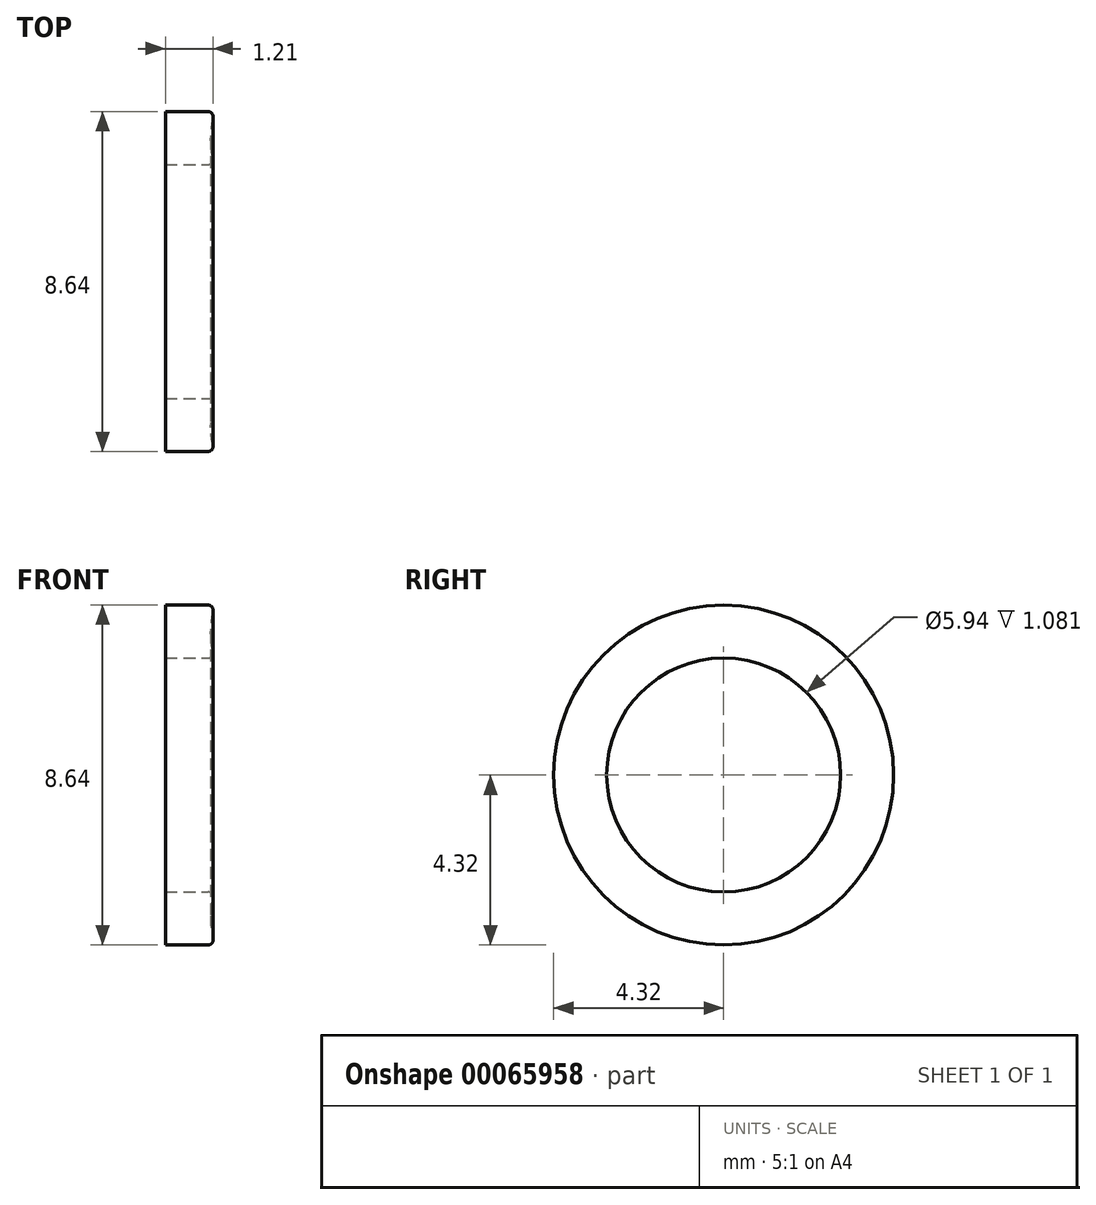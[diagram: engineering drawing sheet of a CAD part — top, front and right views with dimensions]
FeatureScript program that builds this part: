
annotation { "Feature Type Name" : "Feature", "Feature Type Description" : "" }
export const myFeature = defineFeature(function(context is Context, id is Id, definition is map)
    precondition{}
    {
        {
            var Q0;
            Q0=qCreatedBy(makeId("Front.planeOp"),FACE);
            var sketch = newSketch(context, id + "F0", { "sketchPlane" : qUnion([Q0])});
            skLineSegment(sketch, "E0.bottom", {"start": v(-0.17, 4.32) * mm, "end": v(-1.25, 4.32) * mm});
            skLineSegment(sketch, "E0.top", {"start": v(-0.17, 2.97) * mm, "end": v(-1.25, 2.97) * mm});
            skLineSegment(sketch, "E0.right", {"start": v(-1.25, 4.32) * mm, "end": v(-1.25, 2.97) * mm});
            skLineSegment(sketch, "E1", {"start": v(0, 0) * mm, "end": v(-6.16, 0) * mm, "construction": true});
            skArc(sketch, "E2", {"start": v(-0.04, 4.16) * mm, "mid": v(-0.1, 3.64) * mm, "end": v(-0.04, 3.13) * mm});
            skPoint(sketch, "E3.visualSharp", {"position": v(0, 4.32) * mm});
            skArc(sketch, "E3.filletArc", {"start": v(-0.04, 4.16) * mm, "mid": v(-0.07, 4.27) * mm, "end": v(-0.17, 4.32) * mm});
            skPoint(sketch, "E4.visualSharp", {"position": v(0, 2.97) * mm});
            skArc(sketch, "E4.filletArc", {"start": v(-0.17, 2.97) * mm, "mid": v(-0.07, 3.02) * mm, "end": v(-0.04, 3.13) * mm});
            skLineSegment(sketch, "E5", {"start": v(0, 2.97) * mm, "end": v(0, 0) * mm, "construction": true});
            skSolve(sketch);
        }
        {
            var Q0;
            Q0=makeQuery(id+"F0.imprint","IMPRINT",FACE,{"disambiguationData":[TD([[makeQuery(id+"F0.imprint","IMPRINT",EDGE,{"derivedFrom":sQuery(id+"F0.wireOp",EDGE,"E0.bottom")}),1.0]])]});
            var Q1;
            Q1=sQuery(id+"F0.wireOp",EDGE,"E1");
            revolve(context, id + "F1", {"entities" : qUnion([Q0]), "axis" : qUnion([Q1]), "revolveType" : RevolveType.FULL});
        }
    });
